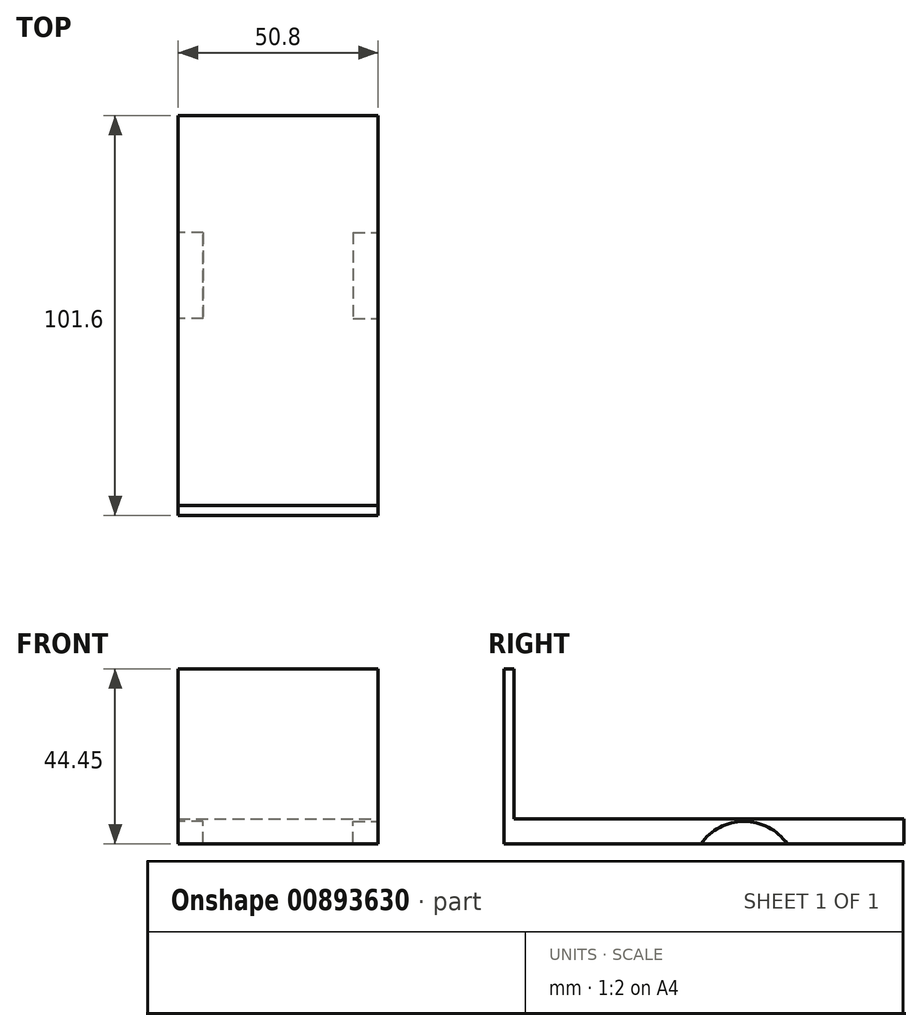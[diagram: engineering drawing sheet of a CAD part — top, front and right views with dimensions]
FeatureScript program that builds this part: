
annotation { "Feature Type Name" : "Feature", "Feature Type Description" : "" }
export const myFeature = defineFeature(function(context is Context, id is Id, definition is map)
    precondition{}
    {
        {
            var Q0;
            Q0=qCreatedBy(makeId("Top.planeOp"),FACE);
            var sketch = newSketch(context, id + "F0", { "sketchPlane" : qUnion([Q0])});
            skLineSegment(sketch, "E0.bottom", {"start": v(-25.4, 50.8) * mm, "end": v(25.4, 50.8) * mm});
            skLineSegment(sketch, "E0.top", {"start": v(-25.4, -50.8) * mm, "end": v(25.4, -50.8) * mm});
            skLineSegment(sketch, "E0.left", {"start": v(-25.4, 50.8) * mm, "end": v(-25.4, -50.8) * mm});
            skLineSegment(sketch, "E0.right", {"start": v(25.4, 50.8) * mm, "end": v(25.4, -50.8) * mm});
            skPoint(sketch, "E0.middle", {"position": v(0, 0) * mm});
            skSolve(sketch);
        }
        {
            var Q0;
            Q0=makeQuery(id+"F0.imprint","IMPRINT",FACE,{"disambiguationData":[TD([[makeQuery(id+"F0.imprint","IMPRINT",EDGE,{"derivedFrom":sQuery(id+"F0.wireOp",EDGE,"E0.bottom")}),-1.0]])]});
            extrude(context, id + "F1", {"entities" : qUnion([Q0]), "depth" : 6.35 * mm, "offsetDistance" : 25.4 * mm});
        }
        {
            var Q0;
            Q0=makeQuery(id+"F1.opExtrude","CAP_FACE",FACE,{"disambiguationData":[OSD([sQuery(id+"F0.wireOp",EDGE,"E0.bottom"),sQuery(id+"F0.wireOp",EDGE,"E0.top"),sQuery(id+"F0.wireOp",EDGE,"E0.left"),sQuery(id+"F0.wireOp",EDGE,"E0.right")])],"isStart":false});
            var sketch = newSketch(context, id + "F2", { "sketchPlane" : qUnion([Q0])});
            skLineSegment(sketch, "E1.bottom", {"start": v(-25.4, -50.8) * mm, "end": v(25.4, -50.8) * mm});
            skLineSegment(sketch, "E1.top", {"start": v(-25.4, -48.26) * mm, "end": v(25.4, -48.26) * mm});
            skLineSegment(sketch, "E1.left", {"start": v(-25.4, -50.8) * mm, "end": v(-25.4, -48.26) * mm});
            skLineSegment(sketch, "E1.right", {"start": v(25.4, -50.8) * mm, "end": v(25.4, -48.26) * mm});
            skSolve(sketch);
        }
        {
            var Q0;
            Q0=makeQuery(id+"F2.imprint","IMPRINT",FACE,{"disambiguationData":[TD([[makeQuery(id+"F2.imprint","IMPRINT",EDGE,{"derivedFrom":sQuery(id+"F2.wireOp",EDGE,"E1.bottom")}),1.0]])]});
            extrude(context, id + "F3", {"entities" : qUnion([Q0]), "operationType" : NewBodyOperationType.ADD, "depth" : 38.1 * mm, "offsetDistance" : 25.4 * mm});
        }
        {
            var Q0;
            Q0=makeQuery(id+"F3.boolean.opBoolean","MERGE",FACE,{"derivedFrom":[makeQuery(id+"F1.opExtrude","SWEPT_FACE",FACE,{"disambiguationData":[OSD([sQuery(id+"F0.wireOp",EDGE,"E0.left")])]}),makeQuery(id+"F3.opExtrude","SWEPT_FACE",FACE,{"disambiguationData":[OSD([sQuery(id+"F2.wireOp",EDGE,"E1.left")])]})]});
            var sketch = newSketch(context, id + "F4", { "sketchPlane" : qUnion([Q0])});
            skCircle(sketch, "E2", {"center": v(-10.16, -7.62) * mm, "radius": 13.34 * mm});
            skSolve(sketch);
        }
        {
            var Q0;
            Q0=makeQuery(id+"F3.boolean.opBoolean","MERGE",FACE,{"derivedFrom":[makeQuery(id+"F1.opExtrude","SWEPT_FACE",FACE,{"disambiguationData":[OSD([sQuery(id+"F0.wireOp",EDGE,"E0.right")])]}),makeQuery(id+"F3.opExtrude","SWEPT_FACE",FACE,{"disambiguationData":[OSD([sQuery(id+"F2.wireOp",EDGE,"E1.right")])]})]});
            var sketch = newSketch(context, id + "F5", { "sketchPlane" : qUnion([Q0])});
            skCircle(sketch, "E3", {"center": v(10.16, -7.62) * mm, "radius": 13.34 * mm});
            skSolve(sketch);
        }
        {
            var Q0;
            {var subQ0=sQuery(id+"F5.wireOp",EDGE,"E3");var subQ1=makeQuery(id+"F1.opExtrude","CAP_EDGE",EDGE,{"disambiguationData":[OSD([sQuery(id+"F0.wireOp",EDGE,"E0.right")])],"isStart":true});var subQ2=makeQuery(id+"F5.imprint","INTERSECT",VERTEX,{"disambiguationData":[OD(0.0)],"derivedFrom":[subQ1,subQ0]});Q0=makeQuery(id+"F5.imprint","IMPRINT",FACE,{"disambiguationData":[TD([[makeQuery(id+"F5.imprint","IMPRINT",EDGE,{"disambiguationData":[TD([[subQ2,-1.0]])],"derivedFrom":subQ0}),1.0]])]});}
            extrude(context, id + "F6", {"entities" : qUnion([Q0]), "operationType" : NewBodyOperationType.REMOVE, "oppositeDirection" : true, "depth" : 6.35 * mm, "offsetDistance" : 25.4 * mm});
        }
        {
            var Q0;
            {var subQ0=sQuery(id+"F4.wireOp",EDGE,"E2");var subQ1=makeQuery(id+"F1.opExtrude","CAP_EDGE",EDGE,{"disambiguationData":[OSD([sQuery(id+"F0.wireOp",EDGE,"E0.left")])],"isStart":true});var subQ2=makeQuery(id+"F4.imprint","INTERSECT",VERTEX,{"disambiguationData":[OD(0.0)],"derivedFrom":[subQ1,subQ0]});Q0=makeQuery(id+"F4.imprint","IMPRINT",FACE,{"disambiguationData":[TD([[makeQuery(id+"F4.imprint","IMPRINT",EDGE,{"disambiguationData":[TD([[subQ2,1.0]])],"derivedFrom":subQ0}),1.0]])]});}
            extrude(context, id + "F7", {"entities" : qUnion([Q0]), "operationType" : NewBodyOperationType.REMOVE, "oppositeDirection" : true, "depth" : 6.35 * mm, "offsetDistance" : 25.4 * mm});
        }
    });
